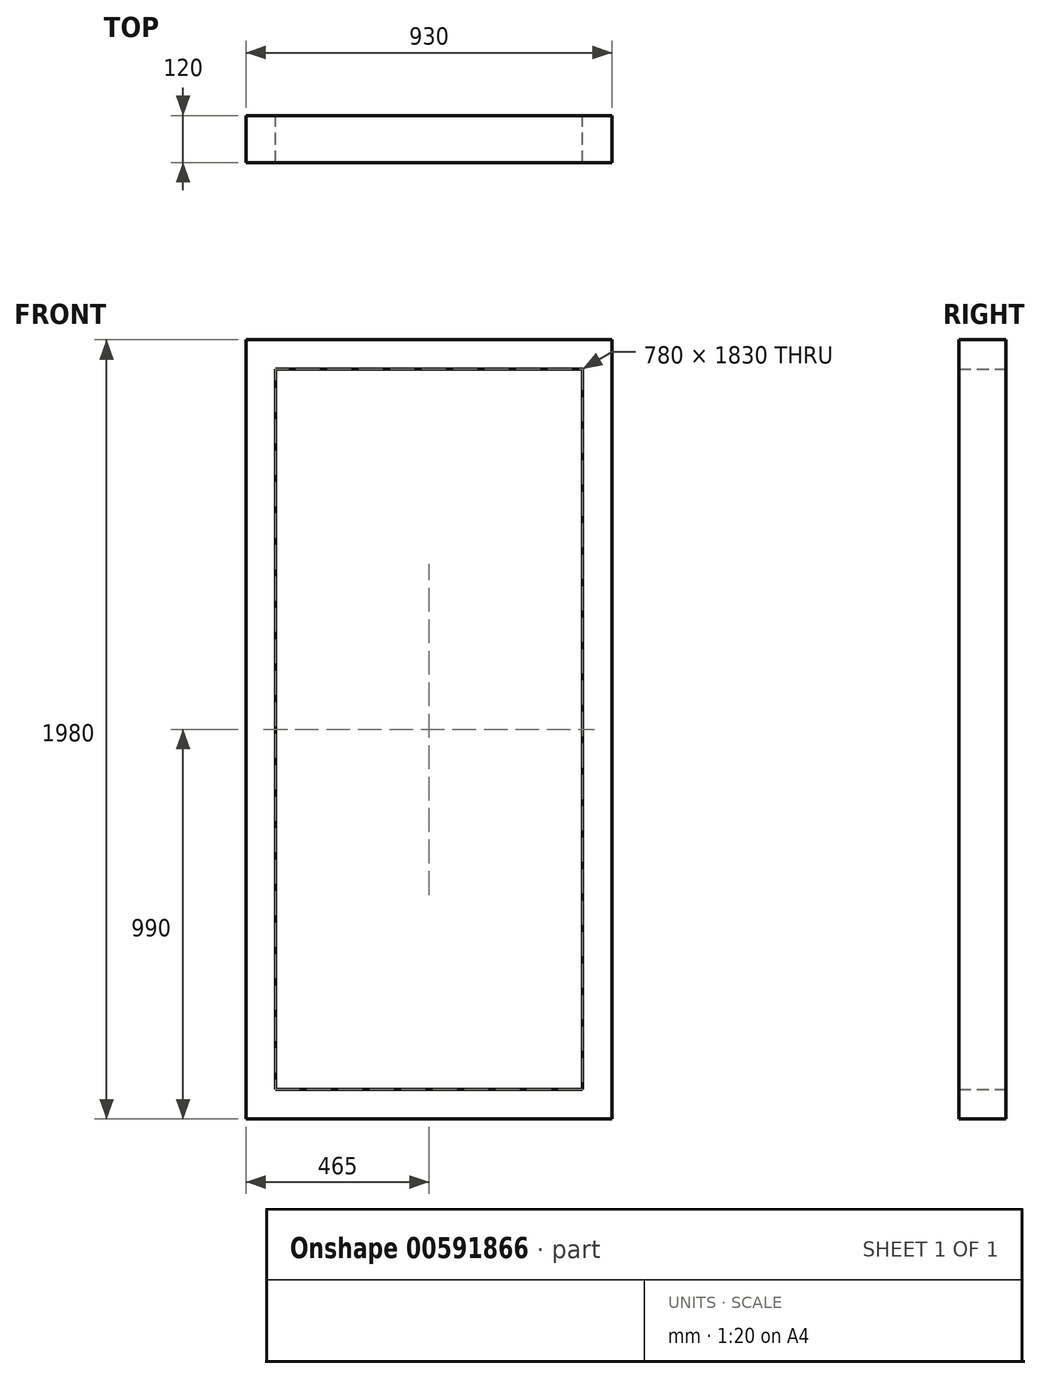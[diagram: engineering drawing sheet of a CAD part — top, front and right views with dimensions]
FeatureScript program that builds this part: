
annotation { "Feature Type Name" : "Feature", "Feature Type Description" : "" }
export const myFeature = defineFeature(function(context is Context, id is Id, definition is map)
    precondition{}
    {
        {
            var Q0;
            Q0=qCreatedBy(makeId("Front.planeOp"),FACE);
            var sketch = newSketch(context, id + "F0", { "sketchPlane" : qUnion([Q0])});
            skLineSegment(sketch, "E0.bottom", {"start": v(0, 0) * mm, "end": v(930, 0) * mm});
            skLineSegment(sketch, "E0.top", {"start": v(0, 1980) * mm, "end": v(930, 1980) * mm});
            skLineSegment(sketch, "E0.left", {"start": v(0, 0) * mm, "end": v(0, 1980) * mm});
            skLineSegment(sketch, "E0.right", {"start": v(930, 0) * mm, "end": v(930, 1980) * mm});
            skLineSegment(sketch, "E1.0", {"start": v(75, 1905) * mm, "end": v(855, 1905) * mm});
            skLineSegment(sketch, "E1.1", {"start": v(75, 75) * mm, "end": v(75, 1905) * mm});
            skLineSegment(sketch, "E1.2", {"start": v(75, 75) * mm, "end": v(855, 75) * mm});
            skLineSegment(sketch, "E1.3", {"start": v(855, 75) * mm, "end": v(855, 1905) * mm});
            skSolve(sketch);
        }
        {
            var Q0;
            Q0=qSketchRegion(id+"F0",true);
            extrude(context, id + "F1", {"entities" : qUnion([Q0]), "depth" : 120 * mm, "offsetDistance" : 25 * mm});
        }
    });
